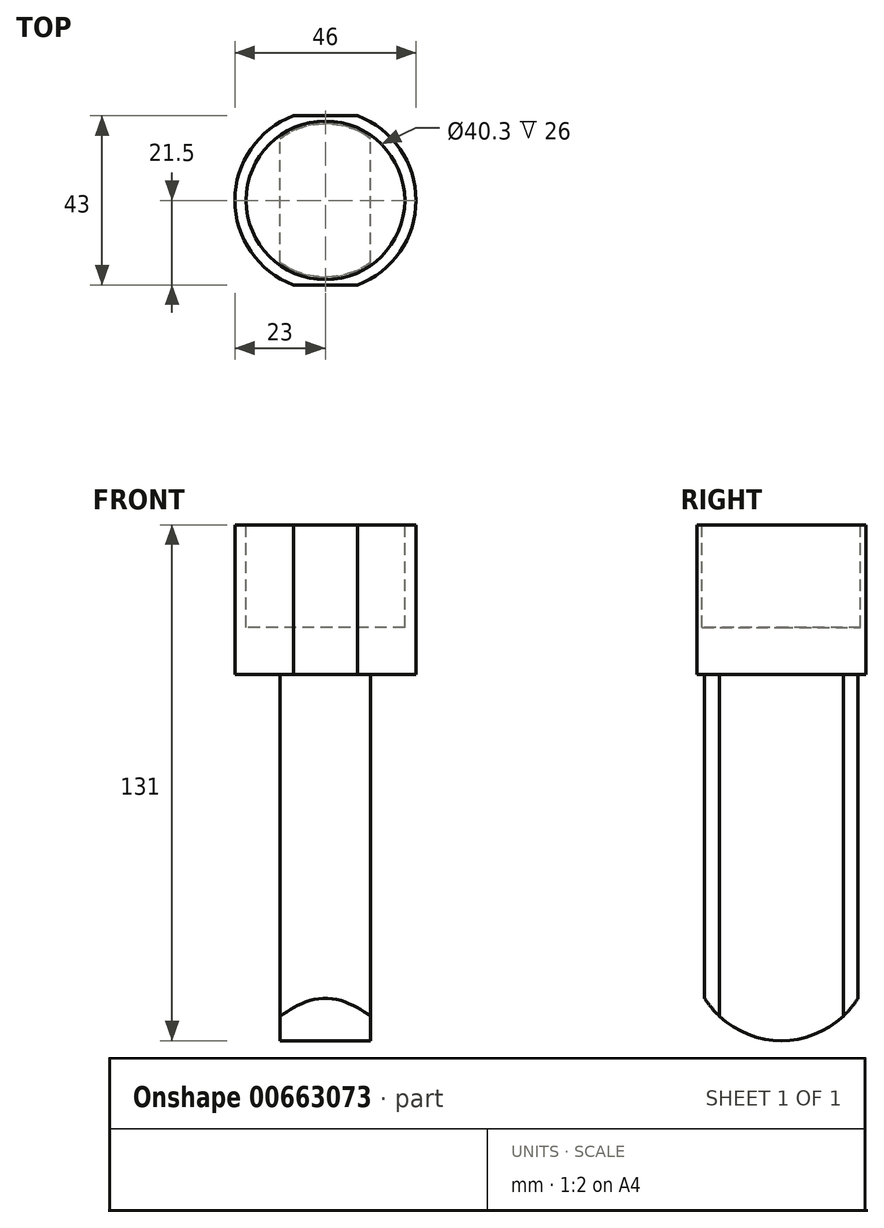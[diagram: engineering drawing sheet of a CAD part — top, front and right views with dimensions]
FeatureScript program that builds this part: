
annotation { "Feature Type Name" : "Feature", "Feature Type Description" : "" }
export const myFeature = defineFeature(function(context is Context, id is Id, definition is map)
    precondition{}
    {
        {
            var Q0;
            Q0=qCreatedBy(makeId("Top.planeOp"),FACE);
            var sketch = newSketch(context, id + "F0", { "sketchPlane" : qUnion([Q0])});
            skArc(sketch, "E0", {"start": v(-8.17, 21.5) * mm, "mid": v(-23, 0) * mm, "end": v(-8.17, -21.5) * mm});
            skLineSegment(sketch, "E1", {"start": v(-8.17, 21.5) * mm, "end": v(8.17, 21.5) * mm});
            skLineSegment(sketch, "E2.MirrorCS", {"start": v(-8.17, -21.5) * mm, "end": v(8.17, -21.5) * mm});
            skArc(sketch, "E3.trimOffspring", {"start": v(8.17, -21.5) * mm, "mid": v(23, 0) * mm, "end": v(8.17, 21.5) * mm});
            skSolve(sketch);
        }
        {
            var Q0;
            Q0=qSketchRegion(id+"F0",true);
            extrude(context, id + "F1", {"entities" : qUnion([Q0]), "depth" : 38 * mm, "offsetDistance" : 25.4 * mm});
        }
        {
            var Q0;
            Q0=makeQuery(id+"F1.opExtrude","CAP_FACE",FACE,{"disambiguationData":[OSD([sQuery(id+"F0.wireOp",EDGE,"E0"),sQuery(id+"F0.wireOp",EDGE,"E1"),sQuery(id+"F0.wireOp",EDGE,"E2.MirrorCS"),sQuery(id+"F0.wireOp",EDGE,"E3.trimOffspring")])],"isStart":false});
            var sketch = newSketch(context, id + "F2", { "sketchPlane" : qUnion([Q0])});
            skCircle(sketch, "E4", {"center": v(0, 0) * mm, "radius": 20.15 * mm});
            skSolve(sketch);
        }
        {
            var Q0;
            Q0=makeQuery(id+"F2.imprint","IMPRINT",FACE,{"disambiguationData":[TD([[makeQuery(id+"F2.imprint","IMPRINT",EDGE,{"derivedFrom":sQuery(id+"F2.wireOp",EDGE,"E4")}),1.0]])]});
            extrude(context, id + "F3", {"entities" : qUnion([Q0]), "operationType" : NewBodyOperationType.REMOVE, "oppositeDirection" : true, "depth" : 26 * mm, "offsetDistance" : 25.4 * mm});
        }
        {
            var Q0;
            Q0=makeQuery(id+"F1.opExtrude","CAP_FACE",FACE,{"disambiguationData":[OSD([sQuery(id+"F0.wireOp",EDGE,"E0"),sQuery(id+"F0.wireOp",EDGE,"E1"),sQuery(id+"F0.wireOp",EDGE,"E2.MirrorCS"),sQuery(id+"F0.wireOp",EDGE,"E3.trimOffspring")])],"isStart":true});
            var sketch = newSketch(context, id + "F4", { "sketchPlane" : qUnion([Q0])});
            skArc(sketch, "E5", {"start": v(-11.5, -15.75) * mm, "mid": v(0, -19.5) * mm, "end": v(11.5, -15.75) * mm});
            skLineSegment(sketch, "E6", {"start": v(-11.5, 15.75) * mm, "end": v(-11.5, -15.75) * mm});
            skLineSegment(sketch, "E7.MirrorCS", {"start": v(11.5, 15.75) * mm, "end": v(11.5, -15.75) * mm});
            skArc(sketch, "E8.trimOffspring", {"start": v(11.5, 15.75) * mm, "mid": v(0, 19.5) * mm, "end": v(-11.5, 15.75) * mm});
            skSolve(sketch);
        }
        {
            var Q0;
            Q0=makeQuery(id+"F4.imprint","IMPRINT",FACE,{"disambiguationData":[TD([[makeQuery(id+"F4.imprint","IMPRINT",EDGE,{"derivedFrom":sQuery(id+"F4.wireOp",EDGE,"E5")}),1.0]])]});
            extrude(context, id + "F5", {"entities" : qUnion([Q0]), "operationType" : NewBodyOperationType.ADD, "depth" : 93 * mm, "offsetDistance" : 25.4 * mm});
        }
        {
            var Q0;
            Q0=qCreatedBy(makeId("Right.planeOp"),FACE);
            var sketch = newSketch(context, id + "F6", { "sketchPlane" : qUnion([Q0])});
            skCircle(sketch, "E9", {"center": v(0, -70) * mm, "radius": 23 * mm});
            skLineSegment(sketch, "E10", {"start": v(-20.75, -79.92) * mm, "end": v(-28.52, -106.52) * mm});
            skLineSegment(sketch, "E11", {"start": v(-28.52, -106.52) * mm, "end": v(30.95, -106.52) * mm});
            skLineSegment(sketch, "E12", {"start": v(30.95, -106.52) * mm, "end": v(21.04, -79.3) * mm});
            skSolve(sketch);
        }
        {
            var Q0;
            {var subQ0=sQuery(id+"F6.wireOp",EDGE,"E10");Q0=makeQuery(id+"F6.imprint","IMPRINT",FACE,{"disambiguationData":[TD([[makeQuery(id+"F6.imprint","IMPRINT",EDGE,{"derivedFrom":subQ0}),1.0]])]});}
            extrude(context, id + "F7", {"entities" : qUnion([Q0]), "operationType" : NewBodyOperationType.REMOVE, "endBound" : BoundingType.THROUGH_ALL, "oppositeDirection" : true, "depth" : 25.4 * mm, "offsetDistance" : 25.4 * mm});
        }
        {
            var Q0;
            {var subQ0=sQuery(id+"F6.wireOp",EDGE,"E12");var subQ1=sQuery(id+"F6.wireOp",EDGE,"E9");var subQ2=makeQuery(id+"F7.opExtrude","CAP_FACE",FACE,{"disambiguationData":[OSD([subQ1,sQuery(id+"F6.wireOp",EDGE,"E10"),sQuery(id+"F6.wireOp",EDGE,"E11"),subQ0])],"isStart":true});var subQ3=sQuery(id+"F4.wireOp",EDGE,"E5");Q0=makeQuery(id+"F7.boolean.opBoolean","COPY",FACE,{"disambiguationData":[TD([makeQuery(id+"F5.opExtrude","SWEPT_FACE",FACE,{"disambiguationData":[OSD([subQ3])]})])],"derivedFrom":subQ2});}
            var Q1;
            {var subQ0=sQuery(id+"F6.wireOp",EDGE,"E10");var subQ1=sQuery(id+"F6.wireOp",EDGE,"E9");var subQ2=makeQuery(id+"F7.opExtrude","CAP_FACE",FACE,{"disambiguationData":[OSD([subQ1,subQ0,sQuery(id+"F6.wireOp",EDGE,"E11"),sQuery(id+"F6.wireOp",EDGE,"E12")])],"isStart":true});var subQ3=sQuery(id+"F4.wireOp",EDGE,"E8.trimOffspring");Q1=makeQuery(id+"F7.boolean.opBoolean","COPY",FACE,{"disambiguationData":[TD([makeQuery(id+"F5.opExtrude","SWEPT_FACE",FACE,{"disambiguationData":[OSD([subQ3])]})])],"derivedFrom":subQ2});}
            extrude(context, id + "F8", {"entities" : qUnion([Q0, Q1]), "operationType" : NewBodyOperationType.REMOVE, "endBound" : BoundingType.THROUGH_ALL, "oppositeDirection" : true, "depth" : 25.4 * mm, "offsetDistance" : 25.4 * mm});
        }
    });
